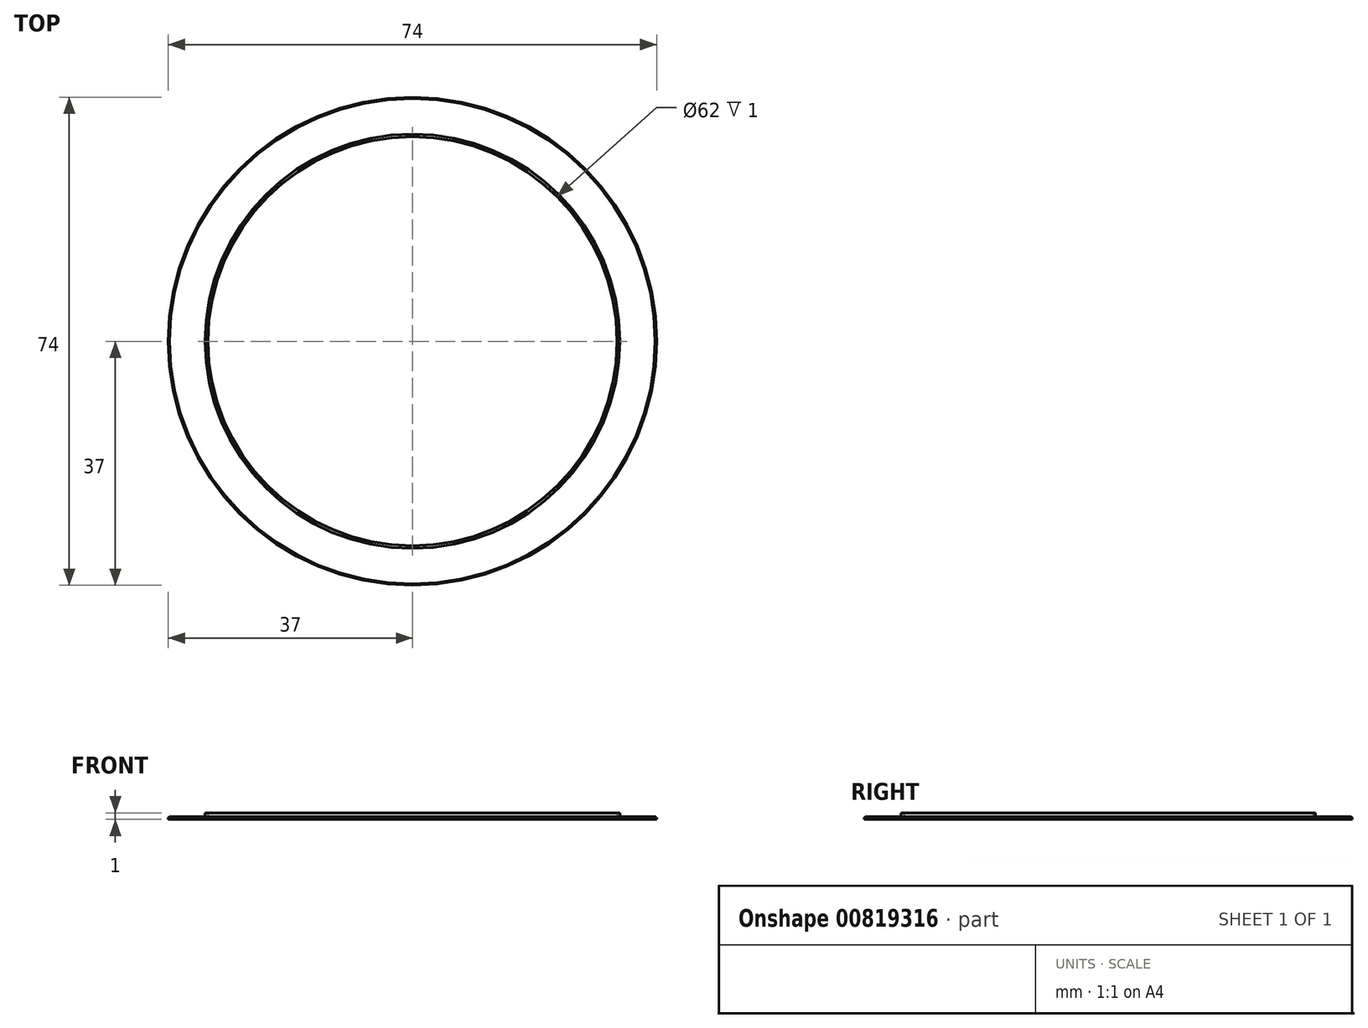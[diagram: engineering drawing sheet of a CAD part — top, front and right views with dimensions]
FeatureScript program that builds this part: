
annotation { "Feature Type Name" : "Feature", "Feature Type Description" : "" }
export const myFeature = defineFeature(function(context is Context, id is Id, definition is map)
    precondition{}
    {
        {
            var Q0;
            Q0=qCreatedBy(makeId("Top.planeOp"),FACE);
            var sketch = newSketch(context, id + "F0", { "sketchPlane" : qUnion([Q0])});
            skCircle(sketch, "E0", {"center": v(0, 0) * mm, "radius": 37 * mm});
            skCircle(sketch, "E1", {"center": v(0, 0) * mm, "radius": 31 * mm});
            skCircle(sketch, "E2", {"center": v(0, 0) * mm, "radius": 31.42 * mm});
            skSolve(sketch);
        }
        {
            var Q0;
            Q0 = qSketchRegion(id + "F0", true);
            var Q1;
            Q1=makeQuery(id+"F0.imprint","IMPRINT",FACE,{"disambiguationData":[TD([[makeQuery(id+"F0.imprint","IMPRINT",EDGE,{"derivedFrom":sQuery(id+"F0.wireOp",EDGE,"E1")}),-1.0]])]});
            extrude(context, id + "F1", {"entities" : qUnion([Q0, Q1]), "depth" : 0.4 * mm, "offsetDistance" : 25 * mm});
        }
        {
            var Q0;
            Q0=makeQuery(id+"F0.imprint","IMPRINT",FACE,{"disambiguationData":[TD([[makeQuery(id+"F0.imprint","IMPRINT",EDGE,{"derivedFrom":sQuery(id+"F0.wireOp",EDGE,"E1")}),-1.0]])]});
            extrude(context, id + "F2", {"entities" : qUnion([Q0]), "operationType" : NewBodyOperationType.ADD, "depth" : 1 * mm, "offsetDistance" : 25 * mm});
        }
        {
            var Q0;
            Q0=makeQuery(id+"F1.opExtrude","CAP_EDGE",EDGE,{"disambiguationData":[OSD([sQuery(id+"F0.wireOp",EDGE,"E0")])],"isStart":false});
            chamfer(context, id + "F3", {"entities" : qUnion([Q0]), "width" : 0.2 * mm, "tangentPropagation" : true});
        }
    });
